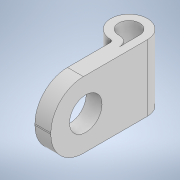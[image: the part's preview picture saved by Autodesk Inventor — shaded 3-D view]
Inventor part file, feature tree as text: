
AUTODESK INVENTOR PART (.ipt)
format: ipt  version: 2021 (Build 250183000, 183)  size: 134,144 bytes
history: native  units: mm
features: sketch x2, extrude x1, hole x1, fillet x1, projected_geometry x1
ambient origin geometry x8: Origin, YZ Plane, XZ Plane, XY Plane, X Axis, Y Axis, Z Axis, Center Point
bodies: Solid1 (feature_tree)
feature tree (6):
  extrude  "Extrusion1"  Depth=3.1mm
  hole  "Hole1"  [1 undecoded]
  fillet  "Fillet1"  Radius=1.2mm
  sketch  "Sketch1"  dims[d0=3.1mm d1=2.8mm]
  sketch  "Sketch2"  dims[d2=14.25mm d3=5.4mm d5=1.2mm d6=0.8mm d7=9.8mm d8=0.0mm d9=11.8mm d10=4.8mm d11=6.0mm d12=4.0mm d13=2.0mm d14=90.0deg d15=8.0mm d16=20.594885mm d17=4.8mm]
  projected_geometry  "Projected Loop1"
note: 1 required parameter value undecoded (feature->parameter linkage not recoverable at this tier; creation-order binding heuristic only, values carry confidence <= 0.55)
